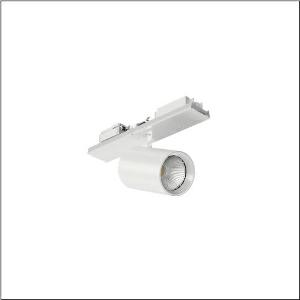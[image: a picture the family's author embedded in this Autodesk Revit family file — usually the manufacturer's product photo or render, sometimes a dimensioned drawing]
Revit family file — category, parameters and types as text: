
# Revit family: licross_spot_31_51sl12da43b
name_source: partatom
category: Lighting Fixtures
units: mm (PartAtom-declared; Revit-internal decimal feet)

## family parameters
Cut with Voids When Loaded = No
Host = Face
Light Source = No
Part Type = Normal
Room Calculation Point = No
Round Connector Dimension = Use Diameter
Shared = No

## types (1)
- --- (1 x LED, 3650 lm, 28.6 W, 4000K)
    Apparent Load = 29 VA
    CIE Flux Codes = 93 97 99 100 100
    Color Rendering = 90
    Color Temperature = 4000K
    Default Elevation = 1800 mm
    Description = Licross Spot 31, directional spotlight, light control with lens, of plastic, LED rated luminous flux: 3.650lm, light colour: 940, with plug, 5-pole, mains connection: 220..240V, AC, 50/60Hz, of aluminium, traffic white (RAL 9016), length: 300mm, diameter: 90mm, protection rating (complete): IP20, insulation class (complete): insulation class I (protective earthing), certification: CE, packaging unit: 1 piece
    Height = 175 mm
    Lamp = 1 x LED
    Lamp Light Flux = 3650 lm
    Lamp Power = 28.6 W
    Lamp count = 1
    Length = 90 mm
    Luminous efficacy = 128 lm/W
    Manufacturer = Siteco
    ModVariant = No
    Model = 51SL12DA43B
    Mounting Place = Ceiling
    Mounting Type = Pendant
    Number of Poles = 1
    OnlyDefault = Yes
    Power Factor = 1
    Product Name = Licross Spot 31
    Product group = directional spotlight
    ProductGroupID = 905
    Protection Class = Protection class I
    Protection Degree = IP 20
    RLX_Detail_Level = 1
    RLX_Emergency_Light_Flux = 0 lm
    RLX_Emergency_Type = 0
    RLX_Emergency_Type_DB = No
    RlxData = <blob elided: 14761 chars, md5=0dea33d4>
    Socket = socket
    Standby Power = 0 W
    System Light Flux = 3650 lm
    System Power = 29 W
    Type Comments = factory setting: luminous flux: 100 % | (ON | ON | ON) | 700 mA
    Type Image = l_1245720.jpg
    URL = http://relux.com
    VarID = @adj_133709
    Voltage = 0 V
    Weight = 0.00 kg
    Width = 0 mm  [stored 0 ft]

note: [stored X ft] marks values corroborated as IEEE doubles in the binary element streams (Revit-internal decimal feet)

## geometry (parser evidence)
native form markers: Sweep x11
no freeform markers — native parametric forms only
